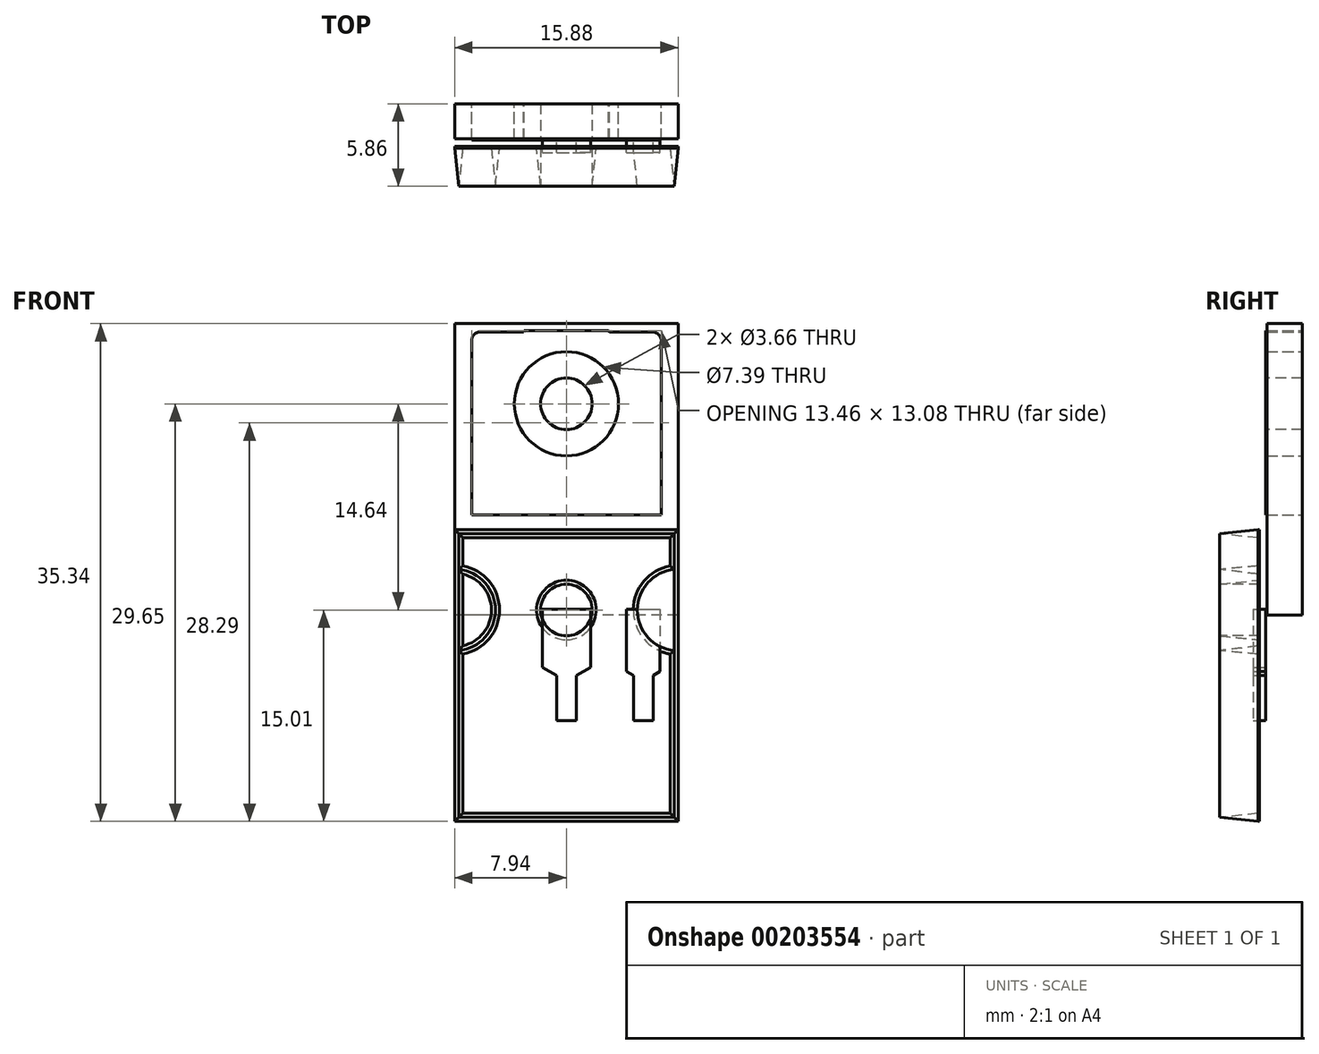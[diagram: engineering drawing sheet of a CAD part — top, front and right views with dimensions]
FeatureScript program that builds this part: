
annotation { "Feature Type Name" : "Feature", "Feature Type Description" : "" }
export const myFeature = defineFeature(function(context is Context, id is Id, definition is map)
    precondition{}
    {
        {
            var Q0;
            Q0=qCreatedBy(makeId("Front.planeOp"),FACE);
            var sketch = newSketch(context, id + "F0", { "sketchPlane" : qUnion([Q0])});
            skLineSegment(sketch, "E0.bottom", {"start": v(7.93, -10.35) * mm, "end": v(-7.94, -10.35) * mm});
            skLineSegment(sketch, "E0.top", {"start": v(7.93, 10.35) * mm, "end": v(-7.93, 10.35) * mm});
            skLineSegment(sketch, "E0.left", {"start": v(7.93, -10.35) * mm, "end": v(7.93, 10.35) * mm});
            skLineSegment(sketch, "E0.right", {"start": v(-7.93, -10.35) * mm, "end": v(-7.93, 10.35) * mm});
            skPoint(sketch, "E0.middle", {"position": v(0, 0) * mm});
            skSolve(sketch);
        }
        {
            var Q0;
            Q0=makeQuery(id+"F0.imprint","IMPRINT",FACE,{"disambiguationData":[TD([[makeQuery(id+"F0.imprint","IMPRINT",EDGE,{"derivedFrom":sQuery(id+"F0.wireOp",EDGE,"E0.bottom")}),-1.0]])]});
            extrude(context, id + "F1", {"entities" : qUnion([Q0]), "depth" : 2.82 * mm});
        }
        {
            var Q0;
            Q0=makeQuery(id+"F1.opExtrude","CAP_EDGE",EDGE,{"disambiguationData":[OSD([sQuery(id+"F0.wireOp",EDGE,"E0.bottom")])],"isStart":false});
            var Q1;
            Q1=makeQuery(id+"F1.opExtrude","CAP_EDGE",EDGE,{"disambiguationData":[OSD([sQuery(id+"F0.wireOp",EDGE,"E0.right")])],"isStart":false});
            var Q2;
            Q2=makeQuery(id+"F1.opExtrude","CAP_EDGE",EDGE,{"disambiguationData":[OSD([sQuery(id+"F0.wireOp",EDGE,"E0.left")])],"isStart":false});
            var Q3;
            Q3=makeQuery(id+"F1.opExtrude","CAP_EDGE",EDGE,{"disambiguationData":[OSD([sQuery(id+"F0.wireOp",EDGE,"E0.top")])],"isStart":false});
            chamfer(context, id + "F2", {"entities" : qUnion([Q0, Q1, Q2, Q3]), "chamferType" : ChamferType.OFFSET_ANGLE, "width" : 2.72 * mm, "oppositeDirection" : false, "angle" : 6 * degree, "tangentPropagation" : true});
        }
        {
            var Q0;
            Q0=makeQuery(id+"F0.imprint","IMPRINT",FACE,{"disambiguationData":[TD([[makeQuery(id+"F0.imprint","IMPRINT",EDGE,{"derivedFrom":sQuery(id+"F0.wireOp",EDGE,"E0.bottom")}),-1.0]])]});
            extrude(context, id + "F3", {"entities" : qUnion([Q0]), "oppositeDirection" : true, "depth" : 2.5 * mm});
        }
        {
            var Q0;
            Q0=makeQuery(id+"F1.opExtrude","CAP_FACE",FACE,{"disambiguationData":[OSD([sQuery(id+"F0.wireOp",EDGE,"E0.bottom"),sQuery(id+"F0.wireOp",EDGE,"E0.top"),sQuery(id+"F0.wireOp",EDGE,"E0.left"),sQuery(id+"F0.wireOp",EDGE,"E0.right")])],"isStart":false});
            var sketch = newSketch(context, id + "F4", { "sketchPlane" : qUnion([Q0])});
            skCircle(sketch, "E1", {"center": v(0, 4.66) * mm, "radius": 1.83 * mm});
            skSolve(sketch);
        }
        {
            var Q0;
            Q0=qSketchRegion(id+"F4",true);
            extrude(context, id + "F5", {"entities" : qUnion([Q0]), "operationType" : NewBodyOperationType.REMOVE, "oppositeDirection" : true, "depth" : 5.3 * mm});
        }
        {
            var Q0;
            Q0=makeQuery(id+"F1.opExtrude","CAP_FACE",FACE,{"disambiguationData":[OSD([sQuery(id+"F0.wireOp",EDGE,"E0.bottom"),sQuery(id+"F0.wireOp",EDGE,"E0.top"),sQuery(id+"F0.wireOp",EDGE,"E0.left"),sQuery(id+"F0.wireOp",EDGE,"E0.right")])],"isStart":false});
            var sketch = newSketch(context, id + "F6", { "sketchPlane" : qUnion([Q0])});
            skArc(sketch, "E2", {"start": v(-7.93, 1.76) * mm, "mid": v(-5.04, 4.66) * mm, "end": v(-7.94, 7.55) * mm});
            skLineSegment(sketch, "E3", {"start": v(-7.93, 4.66) * mm, "end": v(-7.93, -2.18) * mm});
            skLineSegment(sketch, "E4", {"start": v(-7.93, 4.66) * mm, "end": v(-7.93, 8.66) * mm, "construction": true});
            skLineSegment(sketch, "E5", {"start": v(-7.94, 7.55) * mm, "end": v(-7.93, 1.76) * mm});
            skArc(sketch, "E6.MirrorCS", {"start": v(7.93, 1.76) * mm, "mid": v(5.04, 4.66) * mm, "end": v(7.93, 7.55) * mm});
            skLineSegment(sketch, "E7", {"start": v(7.93, 7.55) * mm, "end": v(7.93, 1.76) * mm});
            skLineSegment(sketch, "E8", {"start": v(-7.94, 7.55) * mm, "end": v(-8.42, 7.55) * mm});
            skLineSegment(sketch, "E9", {"start": v(-8.42, 7.55) * mm, "end": v(-8.42, 1.76) * mm});
            skLineSegment(sketch, "E10", {"start": v(-8.42, 1.76) * mm, "end": v(-7.93, 1.76) * mm});
            skLineSegment(sketch, "E11", {"start": v(7.93, 7.55) * mm, "end": v(8.55, 7.55) * mm});
            skLineSegment(sketch, "E12", {"start": v(8.55, 7.55) * mm, "end": v(8.55, 1.76) * mm});
            skLineSegment(sketch, "E13", {"start": v(8.55, 1.76) * mm, "end": v(7.93, 1.76) * mm});
            skSolve(sketch);
        }
        {
            var Q0;
            {var subQ0=sQuery(id+"F6.wireOp",EDGE,"E2");var subQ1=sQuery(id+"F0.wireOp",EDGE,"E0.right");var subQ2=makeQuery(id+"F2.opChamfer","BLEND_EDGE",EDGE,{"blendedFrom":[makeQuery(id+"F1.opExtrude","CAP_EDGE",EDGE,{"disambiguationData":[OSD([subQ1])],"isStart":false}),makeQuery(id+"F1.opExtrude","CAP_FACE",FACE,{"disambiguationData":[OSD([sQuery(id+"F0.wireOp",EDGE,"E0.bottom"),sQuery(id+"F0.wireOp",EDGE,"E0.top"),sQuery(id+"F0.wireOp",EDGE,"E0.left"),subQ1])],"isStart":false})],"blendedInto":[makeQuery(id+"F1.opExtrude","CAP_FACE",FACE,{"disambiguationData":[OSD([sQuery(id+"F0.wireOp",EDGE,"E0.bottom"),sQuery(id+"F0.wireOp",EDGE,"E0.top"),sQuery(id+"F0.wireOp",EDGE,"E0.left"),subQ1])],"isStart":false})]});var subQ3=makeQuery(id+"F6.imprint","INTERSECT",VERTEX,{"disambiguationData":[OD(0.0)],"derivedFrom":[subQ2,subQ0]});Q0=makeQuery(id+"F6.imprint","IMPRINT",FACE,{"disambiguationData":[TD([[makeQuery(id+"F6.imprint","IMPRINT",EDGE,{"disambiguationData":[TD([[subQ3,-1.0]])],"derivedFrom":subQ0}),1.0]])]});}
            var Q1;
            {var subQ0=sQuery(id+"F6.wireOp",EDGE,"E5");Q1=makeQuery(id+"F6.imprint","IMPRINT",FACE,{"disambiguationData":[TD([[makeQuery(id+"F6.imprint","IMPRINT",EDGE,{"derivedFrom":subQ0}),1.0]])]});}
            var Q2;
            {var subQ0=sQuery(id+"F6.wireOp",EDGE,"E7");Q2=makeQuery(id+"F6.imprint","IMPRINT",FACE,{"disambiguationData":[TD([[makeQuery(id+"F6.imprint","IMPRINT",EDGE,{"derivedFrom":subQ0}),-1.0]])]});}
            var Q3;
            {var subQ0=sQuery(id+"F6.wireOp",EDGE,"E6.MirrorCS");var subQ1=sQuery(id+"F0.wireOp",EDGE,"E0.left");var subQ2=makeQuery(id+"F2.opChamfer","BLEND_EDGE",EDGE,{"blendedFrom":[makeQuery(id+"F1.opExtrude","CAP_EDGE",EDGE,{"disambiguationData":[OSD([subQ1])],"isStart":false}),makeQuery(id+"F1.opExtrude","CAP_FACE",FACE,{"disambiguationData":[OSD([sQuery(id+"F0.wireOp",EDGE,"E0.bottom"),sQuery(id+"F0.wireOp",EDGE,"E0.top"),subQ1,sQuery(id+"F0.wireOp",EDGE,"E0.right")])],"isStart":false})],"blendedInto":[makeQuery(id+"F1.opExtrude","CAP_FACE",FACE,{"disambiguationData":[OSD([sQuery(id+"F0.wireOp",EDGE,"E0.bottom"),sQuery(id+"F0.wireOp",EDGE,"E0.top"),subQ1,sQuery(id+"F0.wireOp",EDGE,"E0.right")])],"isStart":false})]});var subQ3=makeQuery(id+"F6.imprint","INTERSECT",VERTEX,{"disambiguationData":[OD(0.0)],"derivedFrom":[subQ2,subQ0]});Q3=makeQuery(id+"F6.imprint","IMPRINT",FACE,{"disambiguationData":[TD([[makeQuery(id+"F6.imprint","IMPRINT",EDGE,{"disambiguationData":[TD([[subQ3,-1.0]])],"derivedFrom":subQ0}),-1.0]])]});}
            var Q4;
            {var subQ0=sQuery(id+"F6.wireOp",EDGE,"E8");Q4=makeQuery(id+"F6.imprint","IMPRINT",FACE,{"disambiguationData":[TD([[makeQuery(id+"F6.imprint","IMPRINT",EDGE,{"derivedFrom":subQ0}),1.0]])]});}
            var Q5;
            Q5=makeQuery(id+"F6.imprint","IMPRINT",FACE,{"disambiguationData":[TD([[makeQuery(id+"F6.imprint","IMPRINT",EDGE,{"derivedFrom":sQuery(id+"F6.wireOp",EDGE,"E7")}),1.0]])]});
            extrude(context, id + "F7", {"entities" : qUnion([Q0, Q1, Q2, Q3, Q4, Q5]), "operationType" : NewBodyOperationType.REMOVE, "oppositeDirection" : true, "depth" : 2.72 * mm, "hasDraft" : true, "draftAngle" : 6 * degree, "draftPullDirection" : true});
        }
        {
            var Q0;
            Q0=makeQuery(id+"F3.opExtrude","CAP_FACE",FACE,{"disambiguationData":[OSD([sQuery(id+"F0.wireOp",EDGE,"E0.bottom"),sQuery(id+"F0.wireOp",EDGE,"E0.top"),sQuery(id+"F0.wireOp",EDGE,"E0.left"),sQuery(id+"F0.wireOp",EDGE,"E0.right")])],"isStart":false});
            var sketch = newSketch(context, id + "F8", { "sketchPlane" : qUnion([Q0])});
            skLineSegment(sketch, "E14", {"start": v(0, -3.24) * mm, "end": v(6.73, -3.24) * mm});
            skLineSegment(sketch, "E15", {"start": v(6.73, -3.24) * mm, "end": v(6.73, 9.14) * mm});
            skLineSegment(sketch, "E16", {"start": v(3.05, 9.75) * mm, "end": v(3, 9.84) * mm});
            skLineSegment(sketch, "E17", {"start": v(3, 9.84) * mm, "end": v(0, 9.84) * mm});
            skArc(sketch, "E18", {"start": v(6.73, 9.14) * mm, "mid": v(6.55, 9.58) * mm, "end": v(6.12, 9.75) * mm});
            skLineSegment(sketch, "E19", {"start": v(6.12, 9.75) * mm, "end": v(3.05, 9.75) * mm});
            skLineSegment(sketch, "E20", {"start": v(6.73, 9.14) * mm, "end": v(5.88, 9.14) * mm, "construction": true});
            skLineSegment(sketch, "E21", {"start": v(6.12, 9.75) * mm, "end": v(6.12, 9.1) * mm, "construction": true});
            skCircle(sketch, "E22", {"center": v(0, 4.66) * mm, "radius": 3.7 * mm});
            skLineSegment(sketch, "E23.MirrorCS", {"start": v(0, 9.84) * mm, "end": v(0, 9.84) * mm});
            skLineSegment(sketch, "E24.MirrorCS", {"start": v(0, -3.24) * mm, "end": v(-6.73, -3.24) * mm});
            skLineSegment(sketch, "E25.MirrorCS", {"start": v(-6.73, -3.24) * mm, "end": v(-6.73, 9.14) * mm});
            skLineSegment(sketch, "E26.MirrorCS", {"start": v(-3.05, 9.75) * mm, "end": v(-3, 9.84) * mm});
            skLineSegment(sketch, "E27.MirrorCS", {"start": v(-6.73, 9.14) * mm, "end": v(-5.88, 9.14) * mm, "construction": true});
            skLineSegment(sketch, "E28.MirrorCS", {"start": v(-6.12, 9.75) * mm, "end": v(-6.12, 9.1) * mm, "construction": true});
            skArc(sketch, "E29.MirrorCS", {"start": v(-6.73, 9.14) * mm, "mid": v(-6.55, 9.58) * mm, "end": v(-6.12, 9.75) * mm});
            skLineSegment(sketch, "E30.MirrorCS", {"start": v(-6.12, 9.75) * mm, "end": v(-3.05, 9.75) * mm});
            skLineSegment(sketch, "E31.MirrorCS", {"start": v(-3, 9.84) * mm, "end": v(0, 9.84) * mm});
            skSolve(sketch);
        }
        {
            var Q0;
            Q0=makeQuery(id+"F8.imprint","IMPRINT",FACE,{"disambiguationData":[TD([[makeQuery(id+"F8.imprint","IMPRINT",EDGE,{"derivedFrom":sQuery(id+"F8.wireOp",EDGE,"E14")}),1.0]])]});
            var Q1;
            Q1=sQuery(id+"F8.wireOp",EDGE,"E19");
            extrude(context, id + "F9", {"entities" : qUnion([Q0]), "surfaceEntities" : qUnion([Q1]), "oppositeDirection" : true, "depth" : 2.59 * mm});
        }
        {
            var Q0;
            Q0=makeQuery(id+"F9.opExtrude","SWEPT_BODY",BODY,{"disambiguationData":[OSD([sQuery(id+"F8.wireOp",EDGE,"E14"),sQuery(id+"F8.wireOp",EDGE,"E15"),sQuery(id+"F8.wireOp",EDGE,"E16"),sQuery(id+"F8.wireOp",EDGE,"E17"),sQuery(id+"F8.wireOp",EDGE,"E18"),sQuery(id+"F8.wireOp",EDGE,"E19"),sQuery(id+"F8.wireOp",EDGE,"E22"),sQuery(id+"F8.wireOp",EDGE,"E24.MirrorCS"),sQuery(id+"F8.wireOp",EDGE,"E25.MirrorCS"),sQuery(id+"F8.wireOp",EDGE,"E26.MirrorCS"),sQuery(id+"F8.wireOp",EDGE,"E29.MirrorCS"),sQuery(id+"F8.wireOp",EDGE,"E30.MirrorCS"),sQuery(id+"F8.wireOp",EDGE,"E31.MirrorCS")])]});
            var Q1;
            Q1=makeQuery(id+"F3.opExtrude","SWEPT_BODY",BODY,{"disambiguationData":[OSD([sQuery(id+"F0.wireOp",EDGE,"E0.bottom"),sQuery(id+"F0.wireOp",EDGE,"E0.top"),sQuery(id+"F0.wireOp",EDGE,"E0.left"),sQuery(id+"F0.wireOp",EDGE,"E0.right")])]});
            booleanBodies(context, id + "F10", {"operationType" : BooleanOperationType.SUBTRACTION, "tools" : qUnion([Q0]), "targets" : qUnion([Q1]), "keepTools" : true});
        }
        {
            assignVariable(context, id + "F11", {"name" : "L1", "anyValue" : 4.3});
        }
        {
            var Q0;
            Q0=qCreatedBy(makeId("Front.planeOp"),FACE);
            var sketch = newSketch(context, id + "F12", { "sketchPlane" : qUnion([Q0])});
            skLineSegment(sketch, "E32", {"start": v(-6.23, -9.94) * mm, "end": v(3.6, -9.94) * mm, "construction": true});
            skLineSegment(sketch, "E33", {"start": v(0, -9.94) * mm, "end": v(-1.72, -9.94) * mm});
            skLineSegment(sketch, "E34", {"start": v(-1.72, -9.94) * mm, "end": v(-1.71, -14.05) * mm});
            skLineSegment(sketch, "E35", {"start": v(-1.72, -14.05) * mm, "end": v(-0.7, -14.64) * mm});
            skLineSegment(sketch, "E36", {"start": v(-0.7, -14.64) * mm, "end": v(-0.7, -17.84) * mm});
            skLineSegment(sketch, "E37", {"start": v(-0.7, -17.84) * mm, "end": v(0, -17.84) * mm});
            skLineSegment(sketch, "E38", {"start": v(0, -9.94) * mm, "end": v(0, -17.84) * mm, "construction": true});
            skLineSegment(sketch, "E39", {"start": v(-0.7, -14.64) * mm, "end": v(-3.26, -14.64) * mm, "construction": true});
            skLineSegment(sketch, "E40.MirrorCS", {"start": v(1.72, -14.05) * mm, "end": v(0.7, -14.64) * mm});
            skLineSegment(sketch, "E41.MirrorCS", {"start": v(0.7, -14.64) * mm, "end": v(0.7, -17.84) * mm});
            skLineSegment(sketch, "E42.MirrorCS", {"start": v(1.72, -9.94) * mm, "end": v(1.71, -14.05) * mm});
            skLineSegment(sketch, "E43.MirrorCS", {"start": v(0, -9.94) * mm, "end": v(1.72, -9.94) * mm});
            skLineSegment(sketch, "E44.MirrorCS", {"start": v(0.7, -17.84) * mm, "end": v(0, -17.84) * mm});
            skLineSegment(sketch, "E45", {"start": v(-5.46, -9.94) * mm, "end": v(-6.65, -9.94) * mm});
            skLineSegment(sketch, "E46", {"start": v(-6.65, -9.94) * mm, "end": v(-6.65, -14.35) * mm});
            skLineSegment(sketch, "E47", {"start": v(-6.65, -14.35) * mm, "end": v(-6.16, -14.64) * mm});
            skLineSegment(sketch, "E48", {"start": v(-6.16, -14.64) * mm, "end": v(-6.16, -17.84) * mm});
            skLineSegment(sketch, "E49", {"start": v(-6.16, -17.84) * mm, "end": v(-5.46, -17.84) * mm});
            skLineSegment(sketch, "E50", {"start": v(-6.16, -14.64) * mm, "end": v(-7.48, -14.64) * mm, "construction": true});
            skLineSegment(sketch, "E51", {"start": v(-5.46, -9.94) * mm, "end": v(-5.46, -18.27) * mm, "construction": true});
            skLineSegment(sketch, "E52.MirrorCS", {"start": v(-4.27, -14.35) * mm, "end": v(-4.76, -14.64) * mm});
            skLineSegment(sketch, "E53.MirrorCS", {"start": v(-4.27, -9.94) * mm, "end": v(-4.27, -14.35) * mm});
            skLineSegment(sketch, "E54.MirrorCS", {"start": v(-4.76, -17.84) * mm, "end": v(-5.46, -17.84) * mm});
            skLineSegment(sketch, "E55.MirrorCS", {"start": v(-4.76, -14.64) * mm, "end": v(-4.76, -17.84) * mm});
            skLineSegment(sketch, "E56.MirrorCS", {"start": v(-5.46, -9.94) * mm, "end": v(-4.27, -9.94) * mm});
            skLineSegment(sketch, "E57.MirrorCS", {"start": v(-10.92, -9.94) * mm, "end": v(-10.92, -17.84) * mm, "construction": true});
            skLineSegment(sketch, "E58.MirrorCS", {"start": v(6.65, -14.35) * mm, "end": v(6.16, -14.64) * mm});
            skLineSegment(sketch, "E59.MirrorCS", {"start": v(6.65, -9.94) * mm, "end": v(6.65, -14.35) * mm});
            skLineSegment(sketch, "E60.MirrorCS", {"start": v(5.46, -9.94) * mm, "end": v(6.65, -9.94) * mm});
            skLineSegment(sketch, "E61.MirrorCS", {"start": v(4.76, -14.64) * mm, "end": v(4.76, -17.84) * mm});
            skLineSegment(sketch, "E62.MirrorCS", {"start": v(5.46, -9.94) * mm, "end": v(4.27, -9.94) * mm});
            skLineSegment(sketch, "E63.MirrorCS", {"start": v(4.27, -14.35) * mm, "end": v(4.76, -14.64) * mm});
            skLineSegment(sketch, "E64.MirrorCS", {"start": v(6.16, -14.64) * mm, "end": v(6.16, -17.84) * mm});
            skLineSegment(sketch, "E65.MirrorCS", {"start": v(6.16, -17.84) * mm, "end": v(5.46, -17.84) * mm});
            skLineSegment(sketch, "E66.MirrorCS", {"start": v(4.27, -9.94) * mm, "end": v(4.27, -14.35) * mm});
            skLineSegment(sketch, "E67.MirrorCS", {"start": v(4.76, -17.84) * mm, "end": v(5.46, -17.84) * mm});
            skSolve(sketch);
        }
        {
            assignVariable(context, id + "F13", {"name" : "c", "anyValue" : 0.89});
        }
        {
            var Q0;
            Q0=makeQuery(id+"F12.imprint","IMPRINT",FACE,{"disambiguationData":[TD([[makeQuery(id+"F12.imprint","IMPRINT",EDGE,{"derivedFrom":sQuery(id+"F12.wireOp",EDGE,"E52.MirrorCS")}),-1.0]])]});
            var Q1;
            Q1=makeQuery(id+"F12.imprint","IMPRINT",FACE,{"disambiguationData":[TD([[makeQuery(id+"F12.imprint","IMPRINT",EDGE,{"derivedFrom":sQuery(id+"F12.wireOp",EDGE,"E33")}),1.0]])]});
            var Q2;
            Q2=makeQuery(id+"F12.imprint","IMPRINT",FACE,{"disambiguationData":[TD([[makeQuery(id+"F12.imprint","IMPRINT",EDGE,{"derivedFrom":sQuery(id+"F12.wireOp",EDGE,"E58.MirrorCS")}),-1.0]])]});
            extrude(context, id + "F14", {"entities" : qUnion([Q0, Q1, Q2]), "depth" : (getVariable(context, 'c')) * mm, "symmetric" : true});
        }
        {
            var Q0;
            Q0=makeQuery(id+"F14.opExtrude","SWEPT_BODY",BODY,{"disambiguationData":[OSD([sQuery(id+"F12.wireOp",EDGE,"E52.MirrorCS"),sQuery(id+"F12.wireOp",EDGE,"E47"),sQuery(id+"F12.wireOp",EDGE,"E55.MirrorCS"),sQuery(id+"F12.wireOp",EDGE,"E49"),sQuery(id+"F12.wireOp",EDGE,"E53.MirrorCS"),sQuery(id+"F12.wireOp",EDGE,"E45"),sQuery(id+"F12.wireOp",EDGE,"E46"),sQuery(id+"F12.wireOp",EDGE,"E54.MirrorCS"),sQuery(id+"F12.wireOp",EDGE,"E48"),sQuery(id+"F12.wireOp",EDGE,"E56.MirrorCS")])]});
            var Q1;
            Q1=makeQuery(id+"F14.opExtrude","SWEPT_BODY",BODY,{"disambiguationData":[OSD([sQuery(id+"F12.wireOp",EDGE,"E33"),sQuery(id+"F12.wireOp",EDGE,"E34"),sQuery(id+"F12.wireOp",EDGE,"E35"),sQuery(id+"F12.wireOp",EDGE,"E36"),sQuery(id+"F12.wireOp",EDGE,"E37"),sQuery(id+"F12.wireOp",EDGE,"E40.MirrorCS"),sQuery(id+"F12.wireOp",EDGE,"E41.MirrorCS"),sQuery(id+"F12.wireOp",EDGE,"E42.MirrorCS"),sQuery(id+"F12.wireOp",EDGE,"E43.MirrorCS"),sQuery(id+"F12.wireOp",EDGE,"E44.MirrorCS")])]});
            var Q2;
            Q2=makeQuery(id+"F14.opExtrude","SWEPT_BODY",BODY,{"disambiguationData":[OSD([sQuery(id+"F12.wireOp",EDGE,"E58.MirrorCS"),sQuery(id+"F12.wireOp",EDGE,"E63.MirrorCS"),sQuery(id+"F12.wireOp",EDGE,"E65.MirrorCS"),sQuery(id+"F12.wireOp",EDGE,"E62.MirrorCS"),sQuery(id+"F12.wireOp",EDGE,"E61.MirrorCS"),sQuery(id+"F12.wireOp",EDGE,"E64.MirrorCS"),sQuery(id+"F12.wireOp",EDGE,"E59.MirrorCS"),sQuery(id+"F12.wireOp",EDGE,"E66.MirrorCS"),sQuery(id+"F12.wireOp",EDGE,"E67.MirrorCS"),sQuery(id+"F12.wireOp",EDGE,"E60.MirrorCS")])]});
            transform(context, id + "F15", {"entities" : qUnion([Q0, Q1, Q2]), "transformType" : TransformType.TRANSLATION_3D, "dx" : 0 * mm, "dy" : (-0.1 - getVariable(context, 'c') / 2) * mm, "dz" : 0 * mm, "makeCopy" : false});
        }
        {
            var Q0;
            Q0=makeQuery(id+"F14.opExtrude","SWEPT_BODY",BODY,{"disambiguationData":[OSD([sQuery(id+"F12.wireOp",EDGE,"E52.MirrorCS"),sQuery(id+"F12.wireOp",EDGE,"E47"),sQuery(id+"F12.wireOp",EDGE,"E55.MirrorCS"),sQuery(id+"F12.wireOp",EDGE,"E49"),sQuery(id+"F12.wireOp",EDGE,"E53.MirrorCS"),sQuery(id+"F12.wireOp",EDGE,"E45"),sQuery(id+"F12.wireOp",EDGE,"E46"),sQuery(id+"F12.wireOp",EDGE,"E54.MirrorCS"),sQuery(id+"F12.wireOp",EDGE,"E48"),sQuery(id+"F12.wireOp",EDGE,"E56.MirrorCS")])]});
            var Q1;
            Q1=makeQuery(id+"F14.opExtrude","SWEPT_BODY",BODY,{"disambiguationData":[OSD([sQuery(id+"F12.wireOp",EDGE,"E33"),sQuery(id+"F12.wireOp",EDGE,"E34"),sQuery(id+"F12.wireOp",EDGE,"E35"),sQuery(id+"F12.wireOp",EDGE,"E36"),sQuery(id+"F12.wireOp",EDGE,"E37"),sQuery(id+"F12.wireOp",EDGE,"E40.MirrorCS"),sQuery(id+"F12.wireOp",EDGE,"E41.MirrorCS"),sQuery(id+"F12.wireOp",EDGE,"E42.MirrorCS"),sQuery(id+"F12.wireOp",EDGE,"E43.MirrorCS"),sQuery(id+"F12.wireOp",EDGE,"E44.MirrorCS")])]});
            var Q2;
            Q2=makeQuery(id+"F14.opExtrude","SWEPT_BODY",BODY,{"disambiguationData":[OSD([sQuery(id+"F12.wireOp",EDGE,"E58.MirrorCS"),sQuery(id+"F12.wireOp",EDGE,"E63.MirrorCS"),sQuery(id+"F12.wireOp",EDGE,"E65.MirrorCS"),sQuery(id+"F12.wireOp",EDGE,"E62.MirrorCS"),sQuery(id+"F12.wireOp",EDGE,"E61.MirrorCS"),sQuery(id+"F12.wireOp",EDGE,"E64.MirrorCS"),sQuery(id+"F12.wireOp",EDGE,"E59.MirrorCS"),sQuery(id+"F12.wireOp",EDGE,"E66.MirrorCS"),sQuery(id+"F12.wireOp",EDGE,"E67.MirrorCS"),sQuery(id+"F12.wireOp",EDGE,"E60.MirrorCS")])]});
            var Q3;
            Q3=makeQuery(id+"F3.opExtrude","SWEPT_BODY",BODY,{"disambiguationData":[OSD([sQuery(id+"F0.wireOp",EDGE,"E0.bottom"),sQuery(id+"F0.wireOp",EDGE,"E0.top"),sQuery(id+"F0.wireOp",EDGE,"E0.left"),sQuery(id+"F0.wireOp",EDGE,"E0.right")])]});
            booleanBodies(context, id + "F16", {"operationType" : BooleanOperationType.SUBTRACTION, "tools" : qUnion([Q0, Q1, Q2]), "targets" : qUnion([Q3]), "keepTools" : true});
        }
        {
            var Q0;
            Q0=makeQuery(id+"F14.opExtrude","SWEPT_BODY",BODY,{"disambiguationData":[OSD([sQuery(id+"F12.wireOp",EDGE,"E52.MirrorCS"),sQuery(id+"F12.wireOp",EDGE,"E47"),sQuery(id+"F12.wireOp",EDGE,"E55.MirrorCS"),sQuery(id+"F12.wireOp",EDGE,"E49"),sQuery(id+"F12.wireOp",EDGE,"E53.MirrorCS"),sQuery(id+"F12.wireOp",EDGE,"E45"),sQuery(id+"F12.wireOp",EDGE,"E46"),sQuery(id+"F12.wireOp",EDGE,"E54.MirrorCS"),sQuery(id+"F12.wireOp",EDGE,"E48"),sQuery(id+"F12.wireOp",EDGE,"E56.MirrorCS")])]});
            var Q1;
            Q1=makeQuery(id+"F3.opExtrude","SWEPT_BODY",BODY,{"disambiguationData":[OSD([sQuery(id+"F0.wireOp",EDGE,"E0.bottom"),sQuery(id+"F0.wireOp",EDGE,"E0.top"),sQuery(id+"F0.wireOp",EDGE,"E0.left"),sQuery(id+"F0.wireOp",EDGE,"E0.right")])]});
            var Q2;
            Q2=makeQuery(id+"F14.opExtrude","SWEPT_BODY",BODY,{"disambiguationData":[OSD([sQuery(id+"F12.wireOp",EDGE,"E33"),sQuery(id+"F12.wireOp",EDGE,"E34"),sQuery(id+"F12.wireOp",EDGE,"E35"),sQuery(id+"F12.wireOp",EDGE,"E36"),sQuery(id+"F12.wireOp",EDGE,"E37"),sQuery(id+"F12.wireOp",EDGE,"E40.MirrorCS"),sQuery(id+"F12.wireOp",EDGE,"E41.MirrorCS"),sQuery(id+"F12.wireOp",EDGE,"E42.MirrorCS"),sQuery(id+"F12.wireOp",EDGE,"E43.MirrorCS"),sQuery(id+"F12.wireOp",EDGE,"E44.MirrorCS")])]});
            var Q3;
            Q3=makeQuery(id+"F14.opExtrude","SWEPT_BODY",BODY,{"disambiguationData":[OSD([sQuery(id+"F12.wireOp",EDGE,"E58.MirrorCS"),sQuery(id+"F12.wireOp",EDGE,"E63.MirrorCS"),sQuery(id+"F12.wireOp",EDGE,"E65.MirrorCS"),sQuery(id+"F12.wireOp",EDGE,"E62.MirrorCS"),sQuery(id+"F12.wireOp",EDGE,"E61.MirrorCS"),sQuery(id+"F12.wireOp",EDGE,"E64.MirrorCS"),sQuery(id+"F12.wireOp",EDGE,"E59.MirrorCS"),sQuery(id+"F12.wireOp",EDGE,"E66.MirrorCS"),sQuery(id+"F12.wireOp",EDGE,"E67.MirrorCS"),sQuery(id+"F12.wireOp",EDGE,"E60.MirrorCS")])]});
            var Q4;
            Q4=makeQuery(id+"F9.opExtrude","SWEPT_BODY",BODY,{"disambiguationData":[OSD([sQuery(id+"F8.wireOp",EDGE,"E14"),sQuery(id+"F8.wireOp",EDGE,"E15"),sQuery(id+"F8.wireOp",EDGE,"E16"),sQuery(id+"F8.wireOp",EDGE,"E17"),sQuery(id+"F8.wireOp",EDGE,"E18"),sQuery(id+"F8.wireOp",EDGE,"E19"),sQuery(id+"F8.wireOp",EDGE,"E22"),sQuery(id+"F8.wireOp",EDGE,"E24.MirrorCS"),sQuery(id+"F8.wireOp",EDGE,"E25.MirrorCS"),sQuery(id+"F8.wireOp",EDGE,"E26.MirrorCS"),sQuery(id+"F8.wireOp",EDGE,"E29.MirrorCS"),sQuery(id+"F8.wireOp",EDGE,"E30.MirrorCS"),sQuery(id+"F8.wireOp",EDGE,"E31.MirrorCS")])]});
            transform(context, id + "F17", {"entities" : qUnion([Q0, Q1, Q2, Q3, Q4]), "transformType" : TransformType.TRANSLATION_3D, "dx" : 0 * mm, "dy" : (0.1 + getVariable(context, 'c') / 2) * mm, "dz" : (10.35 + getVariable(context, 'L1')) * mm, "makeCopy" : false});
        }
    });
